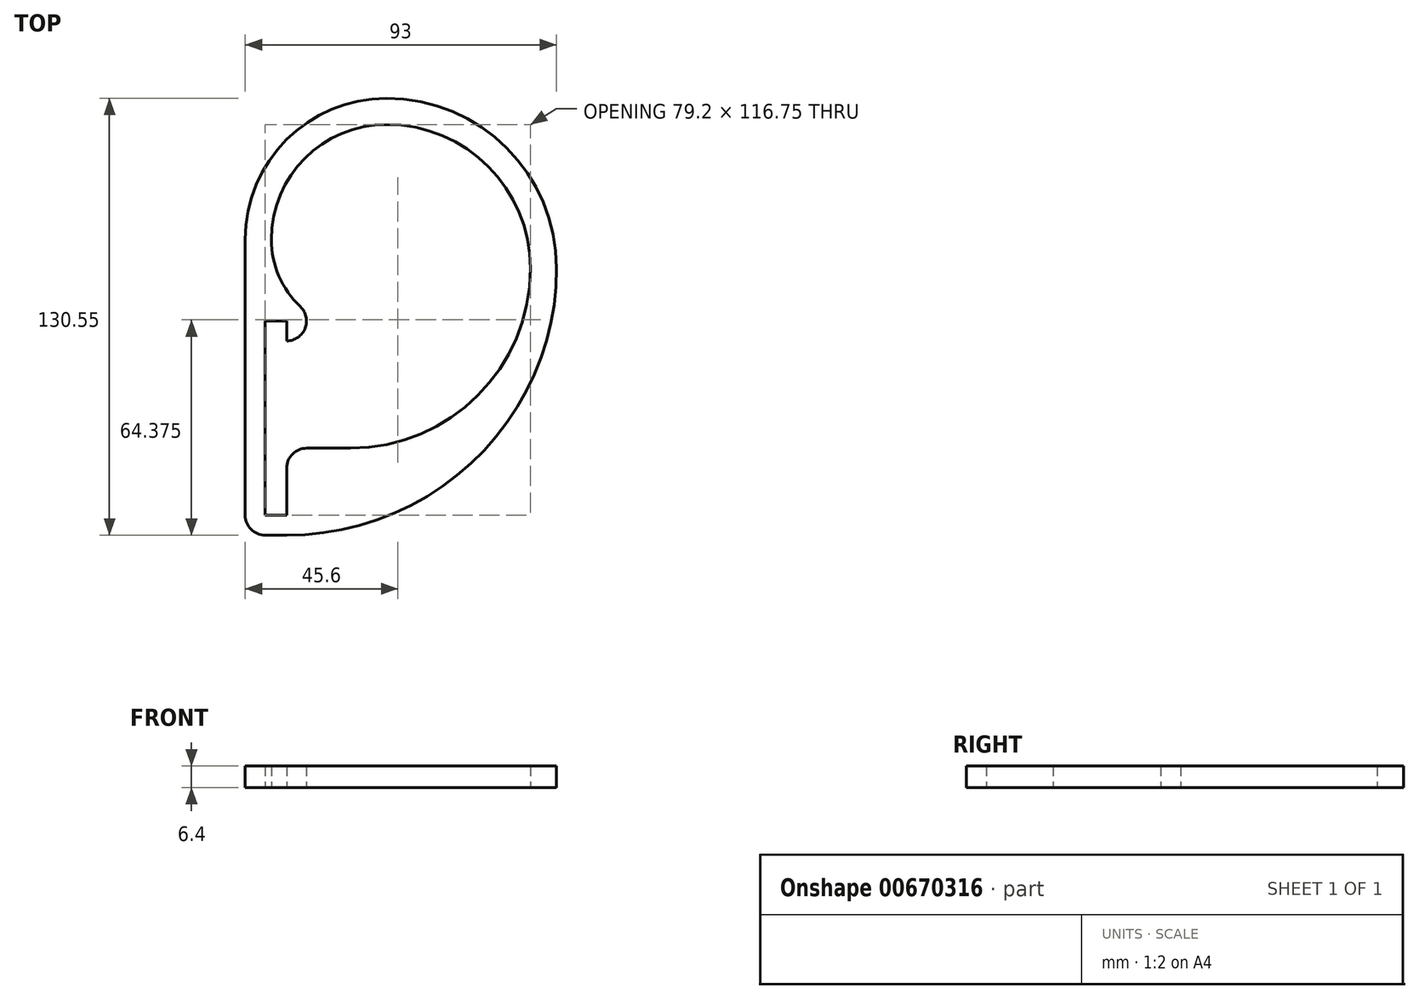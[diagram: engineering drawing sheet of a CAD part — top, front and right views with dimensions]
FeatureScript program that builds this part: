
annotation { "Feature Type Name" : "Feature", "Feature Type Description" : "" }
export const myFeature = defineFeature(function(context is Context, id is Id, definition is map)
    precondition{}
    {
        {
            assignVariable(context, id + "F0", {"name" : "thickness", "anyValue" : 6.4});
        }
        {
            var Q0;
            Q0=qCreatedBy(makeId("Top.planeOp"),FACE);
            var sketch = newSketch(context, id + "F1", { "sketchPlane" : qUnion([Q0])});
            skLineSegment(sketch, "E0", {"start": v(-46.5, -78.05) * mm, "end": v(-46.5, 4.3) * mm});
            skLineSegment(sketch, "E1.bottom", {"start": v(-40.5, -78.05) * mm, "end": v(-34.1, -78.05) * mm});
            skLineSegment(sketch, "E1.top", {"start": v(-40.5, -20.05) * mm, "end": v(-34.1, -20.05) * mm});
            skLineSegment(sketch, "E1.left", {"start": v(-40.5, -78.05) * mm, "end": v(-40.5, -20.05) * mm});
            skLineSegment(sketch, "E1.right", {"start": v(-34.1, -78.05) * mm, "end": v(-34.1, -64.05) * mm});
            skPoint(sketch, "E2", {"position": v(-34.1, -49.05) * mm});
            skPoint(sketch, "E3", {"position": v(-34.1, -40.05) * mm});
            skPoint(sketch, "E4", {"position": v(-34.1, -58.05) * mm});
            skLineSegment(sketch, "E5.trimOffspring", {"start": v(-34.1, -40.05) * mm, "end": v(-34.1, -20.05) * mm, "construction": true});
            skLineSegment(sketch, "E6", {"start": v(-34.1, -40.05) * mm, "end": v(-34.1, -49.05) * mm, "construction": true});
            skLineSegment(sketch, "E7", {"start": v(-34.1, -49.05) * mm, "end": v(-34.1, -58.05) * mm, "construction": true});
            skLineSegment(sketch, "E8", {"start": v(-40.5, -84.05) * mm, "end": v(-34.1, -84.05) * mm});
            skEllipticalArc(sketch, "E9", {});
            skPoint(sketch, "E10", {"position": v(-34.1, -84.05) * mm});
            skPoint(sketch, "E11", {"position": v(46.5, -4.3) * mm});
            skArc(sketch, "E12", {"start": v(-15.05, -58.05) * mm, "mid": v(22.96, -42.3) * mm, "end": v(38.7, -4.3) * mm});
            skArc(sketch, "E13", {"start": v(38.7, -4.3) * mm, "mid": v(26.1, 26.1) * mm, "end": v(-4.3, 38.7) * mm});
            skArc(sketch, "E14", {"start": v(-4.3, 38.7) * mm, "mid": v(-28.62, 28.62) * mm, "end": v(-38.7, 4.3) * mm});
            skArc(sketch, "E15", {"start": v(-38.7, 4.3) * mm, "mid": v(-36.44, -6.61) * mm, "end": v(-30.04, -15.74) * mm});
            skPoint(sketch, "E16", {"position": v(0, 0) * mm});
            skArc(sketch, "E17", {"start": v(-46.5, 4.3) * mm, "mid": v(-34.14, 34.14) * mm, "end": v(-4.3, 46.5) * mm});
            skArc(sketch, "E18", {"start": v(-4.3, 46.5) * mm, "mid": v(31.62, 31.62) * mm, "end": v(46.5, -4.3) * mm});
            skLineSegment(sketch, "E19", {"start": v(-28.1, -58.05) * mm, "end": v(-15.05, -58.05) * mm});
            skPoint(sketch, "E20.visualSharp", {"position": v(-46.5, -84.05) * mm});
            skArc(sketch, "E20.filletArc", {"start": v(-46.5, -78.05) * mm, "mid": v(-44.74, -82.3) * mm, "end": v(-40.5, -84.05) * mm});
            skArc(sketch, "E21", {"start": v(-30.04, -15.74) * mm, "mid": v(-28.6, -22.23) * mm, "end": v(-34.1, -25.97) * mm});
            skLineSegment(sketch, "E22", {"start": v(-34.1, -20.05) * mm, "end": v(-34.1, -25.97) * mm, "construction": true});
            skLineSegment(sketch, "E23", {"start": v(-34.1, -20.05) * mm, "end": v(-34.1, -25.97) * mm});
            skArc(sketch, "E24.filletArc", {"start": v(-28.1, -58.05) * mm, "mid": v(-32.34, -59.8) * mm, "end": v(-34.1, -64.05) * mm});
            const initialGuessF1  = {"E9": [-0.0341, -0.0043, 0, -1, 0.07975, 0.0806, 6.283185307179586, 1.5707963267948966]};
            skSetInitialGuess(sketch, initialGuessF1);
            skSolve(sketch);
        }
        {
            var Q0;
            Q0=makeQuery(id+"F1.imprint","IMPRINT",FACE,{"disambiguationData":[TD([[makeQuery(id+"F1.imprint","IMPRINT",EDGE,{"derivedFrom":sQuery(id+"F1.wireOp",EDGE,"E0")}),-1.0]])]});
            extrude(context, id + "F2", {"entities" : qUnion([Q0]), "depth" : (getVariable(context, 'thickness')) * mm, "offsetDistance" : 25 * mm});
        }
    });
